# Revit family: Plumbing Fixture-FloorDrain_Mifab_C1220C-R
name_source: partatom
category: Plumbing Fixtures
revit_build: Autodesk Revit Structure 2013 (Build: 20120221_2030(x64)
units: mm (PartAtom-declared; Revit-internal decimal feet)

## types (5) — shared parameters
Description = ISOLATION (FLOATING) FLOOR CLEANOUT WITH ADJUSTABLE COVER AND PLUG
Floor Drain Material = Paint - Sherwin Williams Paint - #952C2A - Bellwood Red
Manufacturer = MIFAB
Model = C1220C-R
Top Assembly Height = 8.32 "
URL = WWW.MIFAB.COM
zero-valued in all types: Default Elevation, WFU

## per-type parameters (varying)
| type | Body Height | Pipe Diameter | Pipe Radius | Stainer Diameter | Strainer Radius |
| 3" | 2.75 " | 3 " | 1.5 " | 7 " | 3.5 " |
| 2" | 2.75 " | 2 " | 1 " | 6 " | 3 " |
| 4" | 2.75 " | 4 " | 2 " | 8 " | 4 " |
| 5" | 2.75 " | 5 " | 2.5 " | 9 " | 4.5 " |
| 6" | 3.25 " | 6 " | 3 " | 10 " | 5 " |

## geometry (parser evidence)
native form markers: Blend x3, Sweep x1
no freeform markers — native parametric forms only
